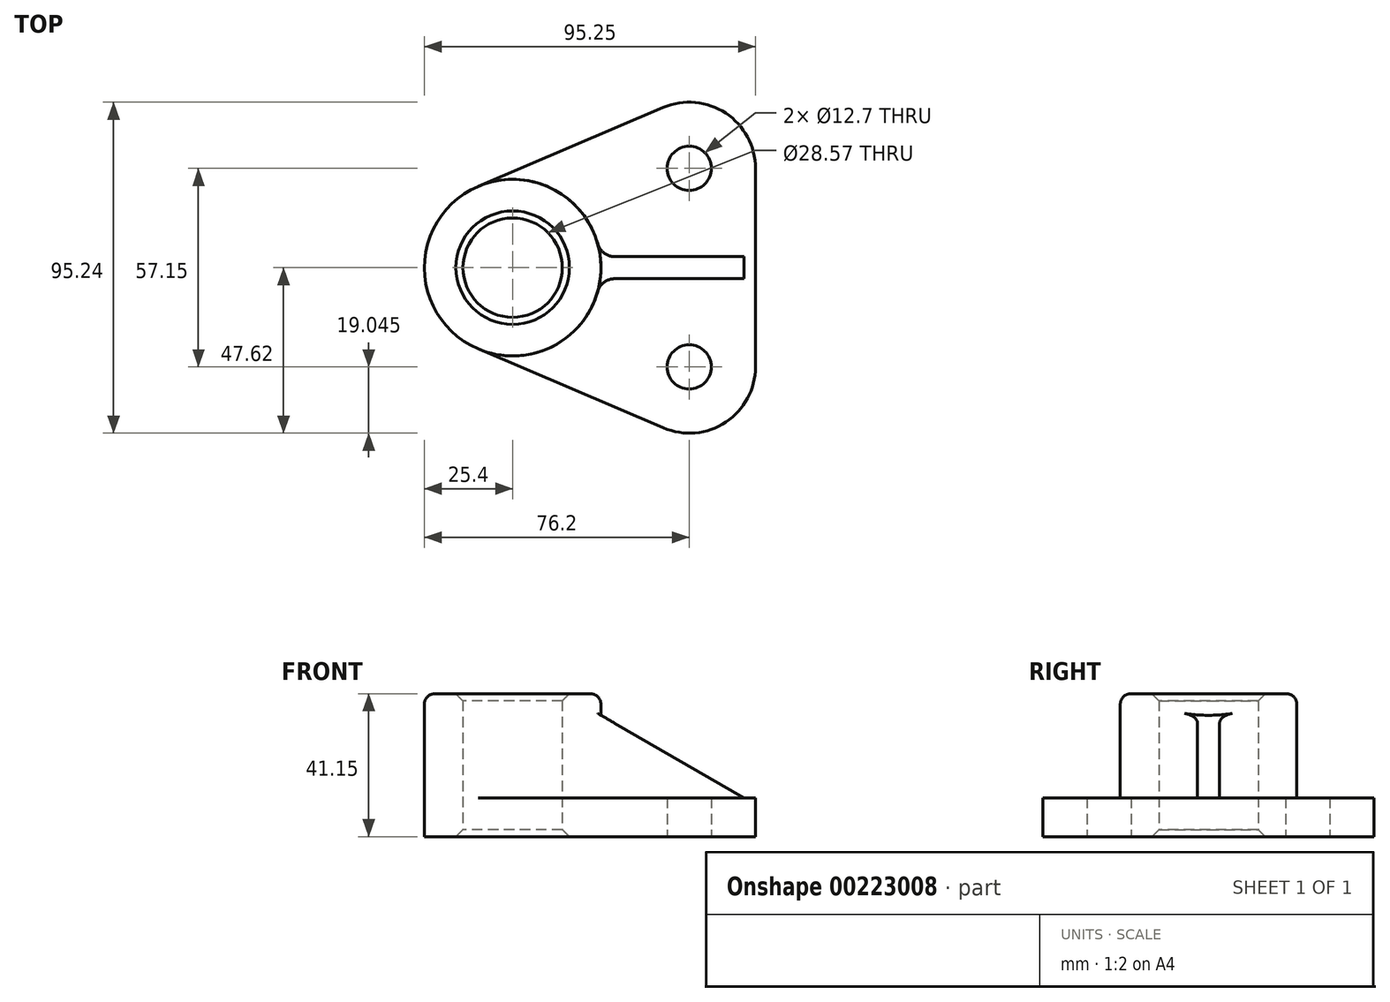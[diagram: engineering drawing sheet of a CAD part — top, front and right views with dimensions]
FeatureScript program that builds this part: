
annotation { "Feature Type Name" : "Feature", "Feature Type Description" : "" }
export const myFeature = defineFeature(function(context is Context, id is Id, definition is map)
    precondition{}
    {
        {
            var Q0;
            Q0=qCreatedBy(makeId("Top.planeOp"),FACE);
            var sketch = newSketch(context, id + "F0", { "sketchPlane" : qUnion([Q0])});
            skLineSegment(sketch, "E0", {"start": v(-66.2, 0) * mm, "end": v(145.62, 0) * mm, "construction": true});
            skCircle(sketch, "E1", {"center": v(0, 0) * mm, "radius": 25.4 * mm});
            skCircle(sketch, "E2", {"center": v(0, 0) * mm, "radius": 14.29 * mm});
            skLineSegment(sketch, "E3", {"start": v(50.8, 0) * mm, "end": v(50.8, -28.58) * mm, "construction": true});
            skLineSegment(sketch, "E4", {"start": v(50.8, 0) * mm, "end": v(50.8, 28.57) * mm, "construction": true});
            skCircle(sketch, "E5", {"center": v(50.8, 28.57) * mm, "radius": 6.35 * mm});
            skCircle(sketch, "E6", {"center": v(50.8, -28.58) * mm, "radius": 6.35 * mm});
            skArc(sketch, "E7", {"start": v(69.85, 28.57) * mm, "mid": v(61.3, 44.47) * mm, "end": v(43.33, 46.1) * mm});
            skArc(sketch, "E8", {"start": v(43.33, -46.1) * mm, "mid": v(61.3, -44.47) * mm, "end": v(69.85, -28.58) * mm});
            skLineSegment(sketch, "E9", {"start": v(-9.97, 23.36) * mm, "end": v(43.33, 46.1) * mm});
            skLineSegment(sketch, "E10", {"start": v(-9.97, -23.36) * mm, "end": v(43.33, -46.1) * mm});
            skLineSegment(sketch, "E11", {"start": v(69.85, 28.57) * mm, "end": v(69.85, -28.58) * mm});
            skSolve(sketch);
        }
        {
            var Q0;
            Q0=makeQuery(id+"F0.imprint","IMPRINT",FACE,{"disambiguationData":[TD([[makeQuery(id+"F0.imprint","IMPRINT",EDGE,{"derivedFrom":sQuery(id+"F0.wireOp",EDGE,"E5")}),-1.0]])]});
            extrude(context, id + "F1", {"entities" : qUnion([Q0]), "depth" : 11.18 * mm});
        }
        {
            var Q0;
            Q0=makeQuery(id+"F0.imprint","IMPRINT",FACE,{"disambiguationData":[TD([[makeQuery(id+"F0.imprint","IMPRINT",EDGE,{"derivedFrom":sQuery(id+"F0.wireOp",EDGE,"E2")}),-1.0]])]});
            extrude(context, id + "F2", {"entities" : qUnion([Q0]), "operationType" : NewBodyOperationType.ADD, "depth" : 41.15 * mm});
        }
        {
            var Q0;
            Q0=qCreatedBy(makeId("Front.planeOp"),FACE);
            var sketch = newSketch(context, id + "F3", { "sketchPlane" : qUnion([Q0])});
            skLineSegment(sketch, "E12", {"start": v(21.05, 37.45) * mm, "end": v(14.57, 11.18) * mm});
            skLineSegment(sketch, "E13.0", {"start": v(14.57, 11.18) * mm, "end": v(43.33, 11.18) * mm});
            skLineSegment(sketch, "E14.0", {"start": v(43.33, 11.18) * mm, "end": v(66.55, 11.18) * mm});
            skLineSegment(sketch, "E15", {"start": v(21.05, 37.45) * mm, "end": v(66.55, 11.18) * mm});
            skPoint(sketch, "E16.orphan", {"position": v(-9.97, 11.18) * mm});
            skSolve(sketch);
        }
        {
            var Q0;
            Q0 = qSketchRegion(id + "F3", true);
            extrude(context, id + "F4", {"entities" : qUnion([Q0]), "operationType" : NewBodyOperationType.ADD, "endBound" : BoundingType.SYMMETRIC, "depth" : 6.35 * mm});
        }
        {
            var Q0;
            Q0=makeQuery(id+"F2.opExtrude","CAP_EDGE",EDGE,{"disambiguationData":[OSD([sQuery(id+"F0.wireOp",EDGE,"E1")])],"isStart":false});
            fillet(context, id + "F5", {"entities" : qUnion([Q0]), "radius" : 3.05 * mm, "tangentPropagation" : true, "allowEdgeOverflow" : false});
        }
        {
            var Q0;
            Q0=makeQuery(id+"F2.opExtrude","CAP_EDGE",EDGE,{"disambiguationData":[OSD([sQuery(id+"F0.wireOp",EDGE,"E2")])],"isStart":false});
            var Q1;
            Q1=makeQuery(id+"F2.opExtrude","CAP_EDGE",EDGE,{"disambiguationData":[OSD([sQuery(id+"F0.wireOp",EDGE,"E2")])],"isStart":true});
            chamfer(context, id + "F6", {"entities" : qUnion([Q0, Q1]), "chamferType" : ChamferType.OFFSET_ANGLE, "width" : 2.03 * mm, "oppositeDirection" : false, "angle" : 45 * degree, "tangentPropagation" : true});
        }
        {
            var Q0;
            {var subQ0=sQuery(id+"F0.wireOp",EDGE,"E10");var subQ1=sQuery(id+"F0.wireOp",EDGE,"E1");Q0=makeQuery(id+"F4.boolean.opBoolean","SPLIT",EDGE,{"disambiguationData":[TD([makeQuery(id+"F1.opExtrude","SWEPT_FACE",FACE,{"disambiguationData":[OSD([subQ0])]})])],"derivedFrom":makeQuery(id+"F1.opExtrude","CAP_EDGE",EDGE,{"disambiguationData":[OSD([subQ1])],"isStart":false})});}
            var Q1;
            Q1=makeQuery(id+"F4.opExtrude","CAP_EDGE",EDGE,{"disambiguationData":[OSD([sQuery(id+"F3.wireOp",EDGE,"E13.0"),sQuery(id+"F3.wireOp",EDGE,"E14.0")])],"isStart":false});
            var Q2;
            Q2=makeQuery(id+"F4.opExtrude","CAP_EDGE",EDGE,{"disambiguationData":[OSD([sQuery(id+"F3.wireOp",EDGE,"E13.0"),sQuery(id+"F3.wireOp",EDGE,"E14.0")])],"isStart":true});
            var Q3;
            {var subQ0=sQuery(id+"F0.wireOp",EDGE,"E9");var subQ1=sQuery(id+"F0.wireOp",EDGE,"E1");Q3=makeQuery(id+"F4.boolean.opBoolean","SPLIT",EDGE,{"disambiguationData":[TD([makeQuery(id+"F1.opExtrude","SWEPT_FACE",FACE,{"disambiguationData":[OSD([subQ0])]})])],"derivedFrom":makeQuery(id+"F1.opExtrude","CAP_EDGE",EDGE,{"disambiguationData":[OSD([subQ1])],"isStart":false})});}
            var Q4;
            Q4=makeQuery(id+"F4.boolean.opBoolean","INTERSECT",EDGE,{"derivedFrom":[makeQuery(id+"F2.opExtrude","SWEPT_FACE",FACE,{"disambiguationData":[OSD([sQuery(id+"F0.wireOp",EDGE,"E1")])]}),makeQuery(id+"F4.opExtrude","CAP_FACE",FACE,{"disambiguationData":[OSD([sQuery(id+"F3.wireOp",EDGE,"E12"),sQuery(id+"F3.wireOp",EDGE,"E13.0"),sQuery(id+"F3.wireOp",EDGE,"E14.0"),sQuery(id+"F3.wireOp",EDGE,"E15")])],"isStart":false})]});
            var Q5;
            Q5=makeQuery(id+"F4.boolean.opBoolean","INTERSECT",EDGE,{"derivedFrom":[makeQuery(id+"F2.opExtrude","SWEPT_FACE",FACE,{"disambiguationData":[OSD([sQuery(id+"F0.wireOp",EDGE,"E1")])]}),makeQuery(id+"F4.opExtrude","CAP_FACE",FACE,{"disambiguationData":[OSD([sQuery(id+"F3.wireOp",EDGE,"E12"),sQuery(id+"F3.wireOp",EDGE,"E13.0"),sQuery(id+"F3.wireOp",EDGE,"E14.0"),sQuery(id+"F3.wireOp",EDGE,"E15")])],"isStart":true})]});
            fillet(context, id + "F7", {"entities" : qUnion([Q0, Q1, Q2, Q3, Q4, Q5]), "radius" : 5.08 * mm, "tangentPropagation" : true, "allowEdgeOverflow" : false});
        }
    });
